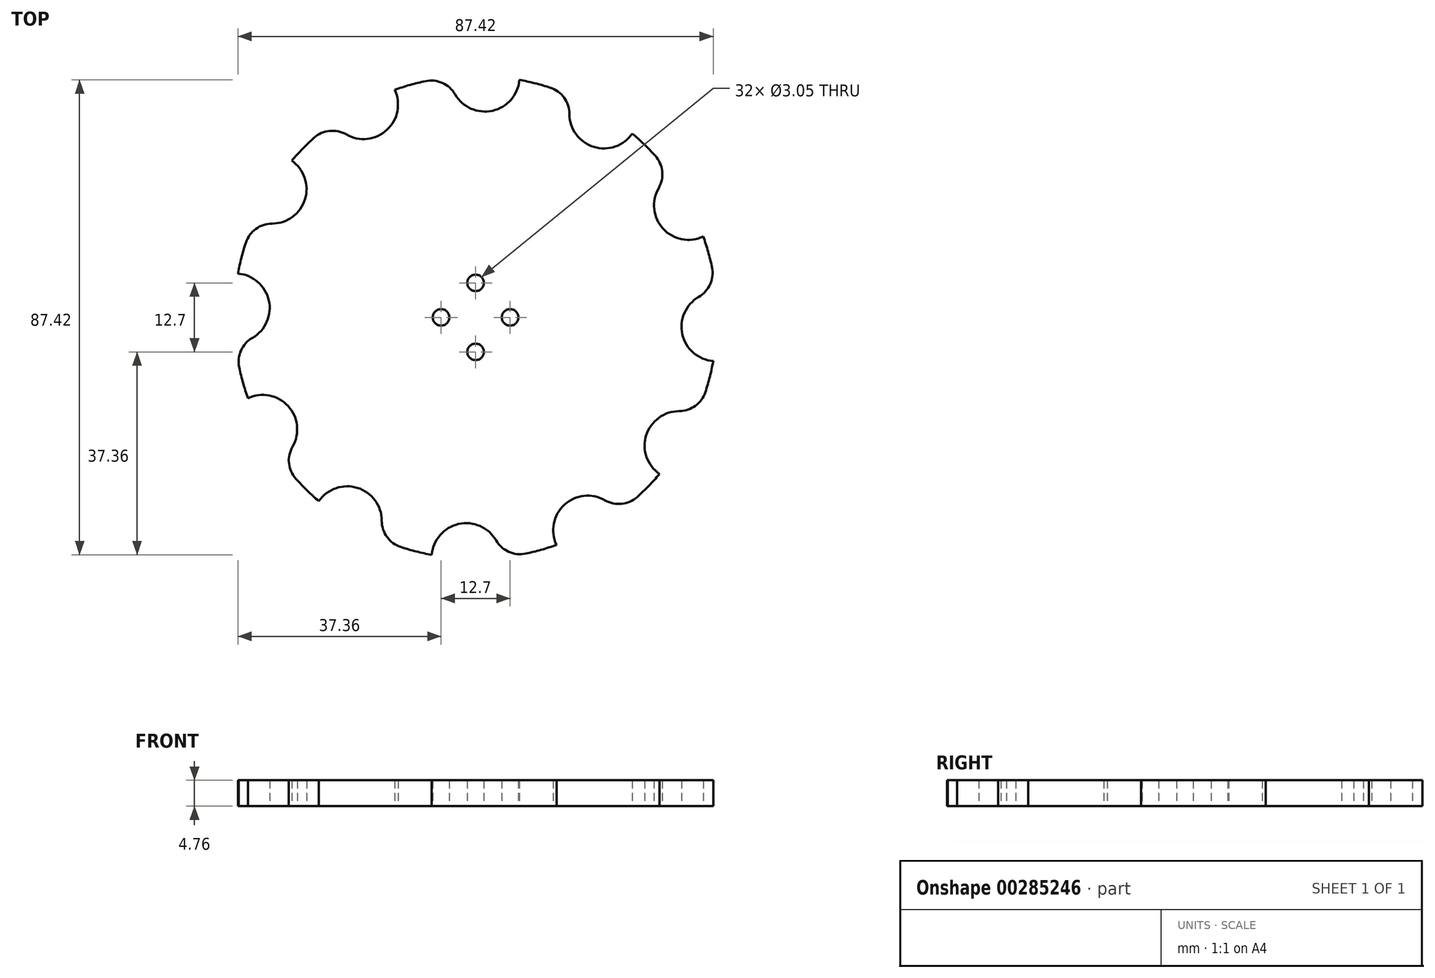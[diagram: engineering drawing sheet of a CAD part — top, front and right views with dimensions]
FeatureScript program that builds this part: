
annotation { "Feature Type Name" : "Feature", "Feature Type Description" : "" }
export const myFeature = defineFeature(function(context is Context, id is Id, definition is map)
    precondition{}
    {
        {
            var Q0;
            Q0=qCreatedBy(makeId("Top.planeOp"),FACE);
            var sketch = newSketch(context, id + "F0", { "sketchPlane" : qUnion([Q0])});
            skArc(sketch, "E0", {"start": v(-9.23, 43.48) * mm, "mid": v(-12.08, 42.78) * mm, "end": v(-14.88, 41.89) * mm});
            skCircle(sketch, "E1", {"center": v(0, 0) * mm, "radius": 6.35 * mm, "construction": true});
            skCircle(sketch, "E2", {"center": v(0, 6.35) * mm, "radius": 1.52 * mm});
            skCircle(sketch, "E3", {"center": v(-6.35, 0) * mm, "radius": 1.52 * mm});
            skCircle(sketch, "E4", {"center": v(0, -6.35) * mm, "radius": 1.52 * mm});
            skCircle(sketch, "E5", {"center": v(6.35, 0) * mm, "radius": 1.52 * mm});
            skArc(sketch, "E6", {"start": v(-3.77, 41.05) * mm, "mid": v(3.12, 38.03) * mm, "end": v(8.06, 43.71) * mm});
            skArc(sketch, "E7.1.0", {"start": v(-23.8, 33.67) * mm, "mid": v(-16.32, 34.5) * mm, "end": v(-14.88, 41.89) * mm});
            skArc(sketch, "E7.2.0", {"start": v(-37.44, 17.26) * mm, "mid": v(-31.38, 21.72) * mm, "end": v(-33.83, 28.83) * mm});
            skArc(sketch, "E7.3.0", {"start": v(-41.05, -3.77) * mm, "mid": v(-38.03, 3.12) * mm, "end": v(-43.71, 8.06) * mm});
            skArc(sketch, "E7.4.0", {"start": v(-33.67, -23.8) * mm, "mid": v(-34.5, -16.32) * mm, "end": v(-41.89, -14.88) * mm});
            skArc(sketch, "E7.5.0", {"start": v(-17.26, -37.44) * mm, "mid": v(-21.72, -31.38) * mm, "end": v(-28.83, -33.83) * mm});
            skArc(sketch, "E7.6.0", {"start": v(3.77, -41.05) * mm, "mid": v(-3.12, -38.03) * mm, "end": v(-8.06, -43.71) * mm});
            skArc(sketch, "E7.7.0", {"start": v(23.8, -33.67) * mm, "mid": v(16.32, -34.5) * mm, "end": v(14.88, -41.89) * mm});
            skArc(sketch, "E7.8.0", {"start": v(37.44, -17.26) * mm, "mid": v(31.38, -21.72) * mm, "end": v(33.83, -28.83) * mm});
            skArc(sketch, "E7.9.0", {"start": v(41.05, 3.77) * mm, "mid": v(38.03, -3.12) * mm, "end": v(43.71, -8.06) * mm});
            skArc(sketch, "E7.10.0", {"start": v(33.67, 23.8) * mm, "mid": v(34.5, 16.32) * mm, "end": v(41.89, 14.88) * mm});
            skArc(sketch, "E7.11.0", {"start": v(17.26, 37.44) * mm, "mid": v(21.72, 31.38) * mm, "end": v(28.83, 33.83) * mm});
            skArc(sketch, "E8.trimOffspring", {"start": v(13.75, 42.27) * mm, "mid": v(10.93, 43.09) * mm, "end": v(8.06, 43.71) * mm});
            skArc(sketch, "E9.trimOffspring", {"start": v(33.04, 29.73) * mm, "mid": v(31, 31.85) * mm, "end": v(28.83, 33.83) * mm});
            skArc(sketch, "E10.trimOffspring", {"start": v(43.48, 9.23) * mm, "mid": v(42.78, 12.08) * mm, "end": v(41.89, 14.88) * mm});
            skArc(sketch, "E11.trimOffspring", {"start": v(42.27, -13.75) * mm, "mid": v(43.09, -10.93) * mm, "end": v(43.71, -8.06) * mm});
            skArc(sketch, "E12.trimOffspring", {"start": v(29.73, -33.04) * mm, "mid": v(31.85, -31) * mm, "end": v(33.83, -28.83) * mm});
            skArc(sketch, "E13.trimOffspring", {"start": v(9.23, -43.48) * mm, "mid": v(12.08, -42.78) * mm, "end": v(14.88, -41.89) * mm});
            skArc(sketch, "E14.trimOffspring", {"start": v(-13.75, -42.27) * mm, "mid": v(-10.93, -43.09) * mm, "end": v(-8.06, -43.71) * mm});
            skArc(sketch, "E15.trimOffspring", {"start": v(-33.04, -29.73) * mm, "mid": v(-31, -31.85) * mm, "end": v(-28.83, -33.83) * mm});
            skArc(sketch, "E16.trimOffspring", {"start": v(-43.48, -9.23) * mm, "mid": v(-42.78, -12.08) * mm, "end": v(-41.89, -14.88) * mm});
            skArc(sketch, "E17.trimOffspring", {"start": v(-42.27, 13.75) * mm, "mid": v(-43.09, 10.93) * mm, "end": v(-43.71, 8.06) * mm});
            skArc(sketch, "E18.trimOffspring", {"start": v(-29.73, 33.04) * mm, "mid": v(-31.85, 31) * mm, "end": v(-33.83, 28.83) * mm});
            skPoint(sketch, "E19.visualSharp", {"position": v(-26.1, 35.97) * mm});
            skArc(sketch, "E19.filletArc", {"start": v(-23.8, 33.67) * mm, "mid": v(-26.86, 34.32) * mm, "end": v(-29.73, 33.04) * mm});
            skPoint(sketch, "E20.visualSharp", {"position": v(-40.6, 18.1) * mm});
            skArc(sketch, "E20.filletArc", {"start": v(-37.44, 17.26) * mm, "mid": v(-40.42, 16.29) * mm, "end": v(-42.27, 13.75) * mm});
            skPoint(sketch, "E21.visualSharp", {"position": v(-44.2, -4.62) * mm});
            skArc(sketch, "E21.filletArc", {"start": v(-41.05, -3.77) * mm, "mid": v(-43.15, -6.1) * mm, "end": v(-43.48, -9.23) * mm});
            skPoint(sketch, "E22.visualSharp", {"position": v(-35.97, -26.1) * mm});
            skArc(sketch, "E22.filletArc", {"start": v(-33.67, -23.8) * mm, "mid": v(-34.32, -26.86) * mm, "end": v(-33.04, -29.73) * mm});
            skPoint(sketch, "E23.visualSharp", {"position": v(-18.1, -40.6) * mm});
            skArc(sketch, "E23.filletArc", {"start": v(-17.26, -37.44) * mm, "mid": v(-16.29, -40.42) * mm, "end": v(-13.75, -42.27) * mm});
            skPoint(sketch, "E24.visualSharp", {"position": v(4.62, -44.2) * mm});
            skArc(sketch, "E24.filletArc", {"start": v(3.77, -41.05) * mm, "mid": v(6.1, -43.15) * mm, "end": v(9.23, -43.48) * mm});
            skPoint(sketch, "E25.visualSharp", {"position": v(26.1, -35.97) * mm});
            skArc(sketch, "E25.filletArc", {"start": v(23.8, -33.67) * mm, "mid": v(26.86, -34.32) * mm, "end": v(29.73, -33.04) * mm});
            skPoint(sketch, "E26.visualSharp", {"position": v(40.6, -18.1) * mm});
            skArc(sketch, "E26.filletArc", {"start": v(37.44, -17.26) * mm, "mid": v(40.42, -16.29) * mm, "end": v(42.27, -13.75) * mm});
            skPoint(sketch, "E27.visualSharp", {"position": v(44.2, 4.62) * mm});
            skArc(sketch, "E27.filletArc", {"start": v(41.05, 3.77) * mm, "mid": v(43.15, 6.1) * mm, "end": v(43.48, 9.23) * mm});
            skPoint(sketch, "E28.visualSharp", {"position": v(35.97, 26.1) * mm});
            skArc(sketch, "E28.filletArc", {"start": v(33.67, 23.8) * mm, "mid": v(34.32, 26.86) * mm, "end": v(33.04, 29.73) * mm});
            skPoint(sketch, "E29.visualSharp", {"position": v(18.1, 40.6) * mm});
            skArc(sketch, "E29.filletArc", {"start": v(17.26, 37.44) * mm, "mid": v(16.29, 40.42) * mm, "end": v(13.75, 42.27) * mm});
            skPoint(sketch, "E30.visualSharp", {"position": v(-4.62, 44.2) * mm});
            skArc(sketch, "E30.filletArc", {"start": v(-3.77, 41.05) * mm, "mid": v(-6.1, 43.15) * mm, "end": v(-9.23, 43.48) * mm});
            skSolve(sketch);
        }
        {
            var Q0;
            Q0 = qSketchRegion(id + "F0", true);
            extrude(context, id + "F1", {"entities" : qUnion([Q0]), "depth" : 4.76 * mm});
        }
    });
